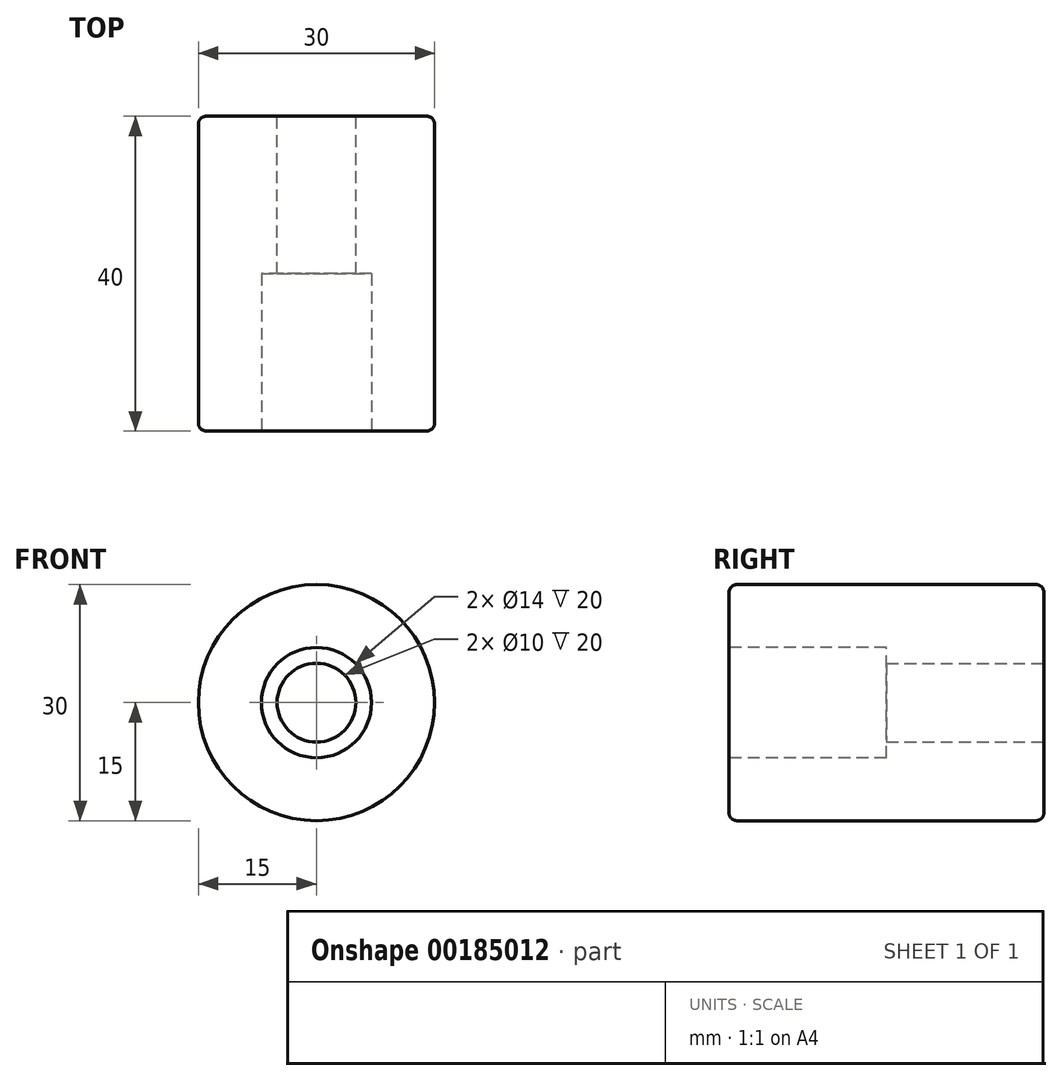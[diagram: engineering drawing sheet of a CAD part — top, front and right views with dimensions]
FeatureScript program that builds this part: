
annotation { "Feature Type Name" : "Feature", "Feature Type Description" : "" }
export const myFeature = defineFeature(function(context is Context, id is Id, definition is map)
    precondition{}
    {
        {
            var Q0;
            Q0=qCreatedBy(makeId("Front.planeOp"),FACE);
            var sketch = newSketch(context, id + "F6", { "sketchPlane" : qUnion([Q0])});
            skCircle(sketch, "E0", {"center": v(0, 0) * mm, "radius": 15 * mm});
            skSolve(sketch);
        }
        {
            var Q0;
            Q0=makeQuery(id+"F6.imprint","IMPRINT",FACE,{"disambiguationData":[TD([[makeQuery(id+"F6.imprint","IMPRINT",EDGE,{"derivedFrom":sQuery(id+"F6.wireOp",EDGE,"E0")}),1.0]])]});
            extrude(context, id + "F0", {"entities" : qUnion([Q0]), "oppositeDirection" : true, "depth" : 40 * mm});
        }
        {
            var Q0;
            Q0=makeQuery(id+"F0.opExtrude","CAP_EDGE",EDGE,{"disambiguationData":[OSD([sQuery(id+"F6.wireOp",EDGE,"E0")])],"isStart":true});
            var Q1;
            Q1=makeQuery(id+"F0.opExtrude","CAP_EDGE",EDGE,{"disambiguationData":[OSD([sQuery(id+"F6.wireOp",EDGE,"E0")])],"isStart":false});
            fillet(context, id + "F1", {"entities" : qUnion([Q0, Q1]), "radius" : 1 * mm, "tangentPropagation" : true, "allowEdgeOverflow" : false});
        }
        {
            var Q0;
            Q0=makeQuery(id+"F0.opExtrude","CAP_FACE",FACE,{"disambiguationData":[OSD([sQuery(id+"F6.wireOp",EDGE,"E0")])],"isStart":true});
            var sketch = newSketch(context, id + "F2", { "sketchPlane" : qUnion([Q0])});
            skPoint(sketch, "E1", {"position": v(0, 0) * mm});
            skCircle(sketch, "E2", {"center": v(0, 0) * mm, "radius": 7 * mm});
            skSolve(sketch);
        }
        {
            var Q0;
            Q0=makeQuery(id+"F2.imprint","IMPRINT",FACE,{"disambiguationData":[TD([[makeQuery(id+"F2.imprint","IMPRINT",EDGE,{"derivedFrom":sQuery(id+"F2.wireOp",EDGE,"E2")}),1.0]])]});
            var Q1;
            Q1=sQuery(id+"F2.wireOp",EDGE,"E2");
            extrude(context, id + "F3", {"entities" : qUnion([Q0]), "operationType" : NewBodyOperationType.REMOVE, "surfaceEntities" : qUnion([Q1]), "oppositeDirection" : true, "depth" : 20 * mm});
        }
        {
            var Q0;
            Q0=makeQuery(id+"F0.opExtrude","CAP_FACE",FACE,{"disambiguationData":[OSD([sQuery(id+"F6.wireOp",EDGE,"E0")])],"isStart":false});
            var sketch = newSketch(context, id + "F4", { "sketchPlane" : qUnion([Q0])});
            skCircle(sketch, "E3", {"center": v(0, 0) * mm, "radius": 5 * mm});
            skSolve(sketch);
        }
        {
            var Q0;
            Q0=makeQuery(id+"F4.imprint","IMPRINT",FACE,{"disambiguationData":[TD([[makeQuery(id+"F4.imprint","IMPRINT",EDGE,{"derivedFrom":sQuery(id+"F4.wireOp",EDGE,"E3")}),1.0]])]});
            extrude(context, id + "F5", {"entities" : qUnion([Q0]), "operationType" : NewBodyOperationType.REMOVE, "oppositeDirection" : true, "depth" : 20 * mm});
        }
    });
